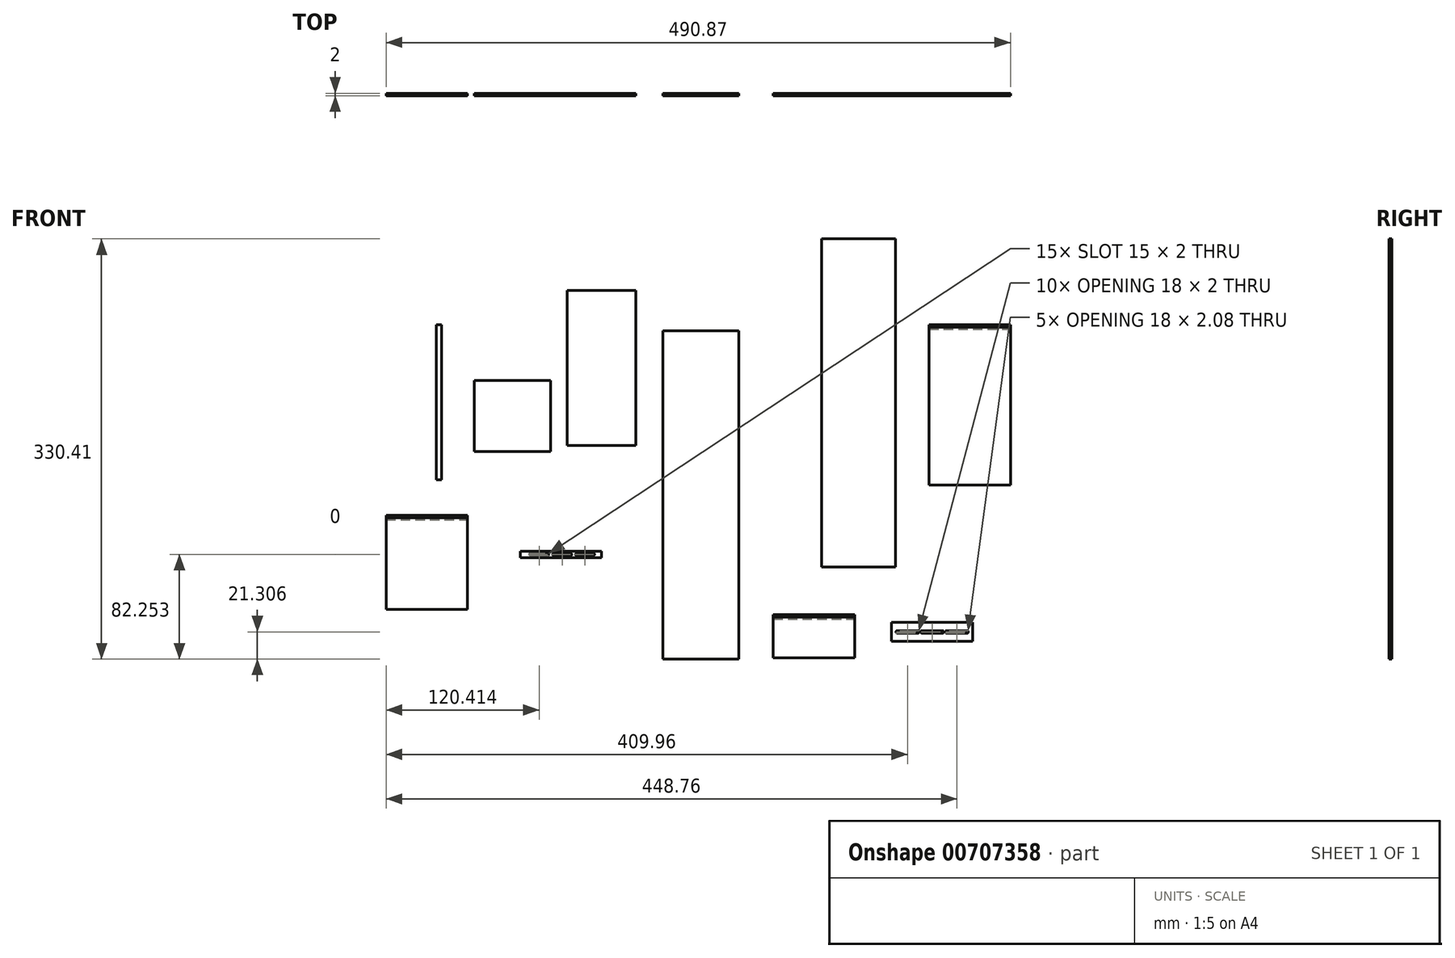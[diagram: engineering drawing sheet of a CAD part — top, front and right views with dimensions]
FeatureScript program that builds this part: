
annotation { "Feature Type Name" : "Feature", "Feature Type Description" : "" }
export const myFeature = defineFeature(function(context is Context, id is Id, definition is map)
    precondition{}
    {
        {
            var Q0;
            Q0=qCreatedBy(makeId("Front.planeOp"),FACE);
            var sketch = newSketch(context, id + "F0", { "sketchPlane" : qUnion([Q0])});
            skLineSegment(sketch, "E0.bottom", {"start": v(-75.81, 223.14) * mm, "end": v(-15.81, 223.14) * mm});
            skLineSegment(sketch, "E0.top", {"start": v(-75.81, -34.86) * mm, "end": v(-15.81, -34.86) * mm});
            skLineSegment(sketch, "E0.left", {"start": v(-75.81, 223.14) * mm, "end": v(-75.81, -34.86) * mm});
            skLineSegment(sketch, "E0.right", {"start": v(-15.81, 223.14) * mm, "end": v(-15.81, -34.86) * mm});
            skSolve(sketch);
        }
        {
            var Q0;
            Q0=makeQuery(id+"F0.imprint","IMPRINT",FACE,{"disambiguationData":[TD([[makeQuery(id+"F0.imprint","IMPRINT",EDGE,{"derivedFrom":sQuery(id+"F0.wireOp",EDGE,"E0.bottom")}),-1.0]])]});
            extrude(context, id + "F1", {"entities" : qUnion([Q0]), "depth" : 2 * mm});
        }
        {
            var Q0;
            Q0=qCreatedBy(makeId("Front.planeOp"),FACE);
            var sketch = newSketch(context, id + "F2", { "sketchPlane" : qUnion([Q0])});
            skLineSegment(sketch, "E1.bottom", {"start": v(49.18, 295.55) * mm, "end": v(107.18, 295.55) * mm});
            skLineSegment(sketch, "E1.top", {"start": v(49.18, 37.55) * mm, "end": v(107.18, 37.55) * mm});
            skLineSegment(sketch, "E1.left", {"start": v(49.18, 295.55) * mm, "end": v(49.18, 37.55) * mm});
            skLineSegment(sketch, "E1.right", {"start": v(107.18, 295.55) * mm, "end": v(107.18, 37.55) * mm});
            skSolve(sketch);
        }
        {
            var Q0;
            Q0=qSketchRegion(id+"F2",true);
            extrude(context, id + "F3", {"entities" : qUnion([Q0]), "depth" : 2 * mm});
        }
        {
            var Q0;
            Q0=qCreatedBy(makeId("Front.planeOp"),FACE);
            var sketch = newSketch(context, id + "F4", { "sketchPlane" : qUnion([Q0])});
            skLineSegment(sketch, "E2.bottom", {"start": v(-223.94, 184.27) * mm, "end": v(-163.94, 184.27) * mm});
            skLineSegment(sketch, "E2.top", {"start": v(-223.94, 128.27) * mm, "end": v(-163.94, 128.27) * mm});
            skLineSegment(sketch, "E2.left", {"start": v(-223.94, 184.27) * mm, "end": v(-223.94, 128.27) * mm});
            skLineSegment(sketch, "E2.right", {"start": v(-163.94, 184.27) * mm, "end": v(-163.94, 128.27) * mm});
            skSolve(sketch);
        }
        {
            var Q0;
            Q0=makeQuery(id+"F4.imprint","IMPRINT",FACE,{"disambiguationData":[TD([[makeQuery(id+"F4.imprint","IMPRINT",EDGE,{"derivedFrom":sQuery(id+"F4.wireOp",EDGE,"E2.bottom")}),-1.0]])]});
            extrude(context, id + "F5", {"entities" : qUnion([Q0]), "depth" : 2 * mm});
        }
        {
            var Q0;
            Q0=qCreatedBy(makeId("Front.planeOp"),FACE);
            var sketch = newSketch(context, id + "F6", { "sketchPlane" : qUnion([Q0])});
            skLineSegment(sketch, "E3.bottom", {"start": v(-187.77, 49.9) * mm, "end": v(-123.77, 49.9) * mm});
            skLineSegment(sketch, "E3.top", {"start": v(-187.77, 44.9) * mm, "end": v(-123.77, 44.9) * mm});
            skLineSegment(sketch, "E3.left", {"start": v(-187.77, 49.9) * mm, "end": v(-187.77, 44.9) * mm});
            skLineSegment(sketch, "E3.right", {"start": v(-123.77, 49.9) * mm, "end": v(-123.77, 44.9) * mm});
            skLineSegment(sketch, "E4.bottom", {"start": v(-179.36, 48.4) * mm, "end": v(-166.36, 48.4) * mm});
            skLineSegment(sketch, "E4.top", {"start": v(-179.36, 46.4) * mm, "end": v(-166.36, 46.4) * mm});
            skLineSegment(sketch, "E4.left", {"start": v(-180.36, 47.4) * mm, "end": v(-180.36, 47.4) * mm});
            skLineSegment(sketch, "E4.right", {"start": v(-165.36, 47.4) * mm, "end": v(-165.36, 47.4) * mm});
            skPoint(sketch, "E5.visualSharp", {"position": v(-180.36, 48.4) * mm});
            skArc(sketch, "E5.filletArc", {"start": v(-179.36, 48.4) * mm, "mid": v(-180.06, 48.1) * mm, "end": v(-180.36, 47.4) * mm});
            skPoint(sketch, "E6.visualSharp", {"position": v(-165.36, 48.4) * mm});
            skArc(sketch, "E6.filletArc", {"start": v(-165.36, 47.4) * mm, "mid": v(-165.65, 48.1) * mm, "end": v(-166.36, 48.4) * mm});
            skPoint(sketch, "E7.visualSharp", {"position": v(-165.36, 46.4) * mm});
            skArc(sketch, "E7.filletArc", {"start": v(-166.36, 46.4) * mm, "mid": v(-165.65, 46.69) * mm, "end": v(-165.36, 47.4) * mm});
            skPoint(sketch, "E8.visualSharp", {"position": v(-180.36, 46.4) * mm});
            skArc(sketch, "E8.filletArc", {"start": v(-180.36, 47.4) * mm, "mid": v(-180.06, 46.69) * mm, "end": v(-179.36, 46.4) * mm});
            skArc(sketch, "E9.1.0.0", {"start": v(-161.36, 48.4) * mm, "mid": v(-162.06, 48.1) * mm, "end": v(-162.36, 47.4) * mm});
            skLineSegment(sketch, "E9.1.0.1", {"start": v(-161.36, 48.4) * mm, "end": v(-148.36, 48.4) * mm});
            skArc(sketch, "E9.1.0.2", {"start": v(-147.36, 47.4) * mm, "mid": v(-147.65, 48.1) * mm, "end": v(-148.36, 48.4) * mm});
            skArc(sketch, "E9.1.0.3", {"start": v(-148.36, 46.4) * mm, "mid": v(-147.65, 46.69) * mm, "end": v(-147.36, 47.4) * mm});
            skLineSegment(sketch, "E9.1.0.4", {"start": v(-161.36, 46.4) * mm, "end": v(-148.36, 46.4) * mm});
            skArc(sketch, "E9.1.0.5", {"start": v(-162.36, 47.4) * mm, "mid": v(-162.06, 46.69) * mm, "end": v(-161.36, 46.4) * mm});
            skArc(sketch, "E9.2.0.0", {"start": v(-143.36, 48.4) * mm, "mid": v(-144.06, 48.1) * mm, "end": v(-144.36, 47.4) * mm});
            skLineSegment(sketch, "E9.2.0.1", {"start": v(-143.36, 48.4) * mm, "end": v(-130.36, 48.4) * mm});
            skArc(sketch, "E9.2.0.2", {"start": v(-129.36, 47.4) * mm, "mid": v(-129.65, 48.1) * mm, "end": v(-130.36, 48.4) * mm});
            skArc(sketch, "E9.2.0.3", {"start": v(-130.36, 46.4) * mm, "mid": v(-129.65, 46.69) * mm, "end": v(-129.36, 47.4) * mm});
            skLineSegment(sketch, "E9.2.0.4", {"start": v(-143.36, 46.4) * mm, "end": v(-130.36, 46.4) * mm});
            skArc(sketch, "E9.2.0.5", {"start": v(-144.36, 47.4) * mm, "mid": v(-144.06, 46.69) * mm, "end": v(-143.36, 46.4) * mm});
            skLineSegment(sketch, "E9.direction1", {"start": v(-180.36, 47.4) * mm, "end": v(-162.36, 47.4) * mm, "construction": true});
            skSolve(sketch);
        }
        {
            var Q0;
            Q0=qSketchRegion(id+"F6",true);
            extrude(context, id + "F7", {"entities" : qUnion([Q0]), "depth" : 2 * mm});
        }
        {
            var Q0;
            Q0=qCreatedBy(makeId("Front.planeOp"),FACE);
            var sketch = newSketch(context, id + "F8", { "sketchPlane" : qUnion([Q0])});
            skLineSegment(sketch, "E10.bottom", {"start": v(-293.27, 78.23) * mm, "end": v(-229.27, 78.23) * mm});
            skLineSegment(sketch, "E10.top", {"start": v(-293.27, 4.23) * mm, "end": v(-229.27, 4.23) * mm});
            skLineSegment(sketch, "E10.left", {"start": v(-293.27, 78.23) * mm, "end": v(-293.27, 4.23) * mm});
            skLineSegment(sketch, "E10.right", {"start": v(-229.27, 78.23) * mm, "end": v(-229.27, 4.23) * mm});
            skSolve(sketch);
        }
        {
            var Q0;
            Q0=makeQuery(id+"F8.imprint","IMPRINT",FACE,{"disambiguationData":[TD([[makeQuery(id+"F8.imprint","IMPRINT",EDGE,{"derivedFrom":sQuery(id+"F8.wireOp",EDGE,"E10.bottom")}),-1.0]])]});
            extrude(context, id + "F9", {"entities" : qUnion([Q0]), "depth" : 2 * mm});
        }
        {
            var Q0;
            Q0=qCreatedBy(makeId("Front.planeOp"),FACE);
            var sketch = newSketch(context, id + "F10", { "sketchPlane" : qUnion([Q0])});
            skLineSegment(sketch, "E11.bottom", {"start": v(104.02, -5.93) * mm, "end": v(168.02, -5.93) * mm});
            skLineSegment(sketch, "E11.top", {"start": v(104.02, -20.93) * mm, "end": v(168.02, -20.93) * mm});
            skLineSegment(sketch, "E11.left", {"start": v(104.02, -5.93) * mm, "end": v(104.02, -20.93) * mm});
            skLineSegment(sketch, "E11.right", {"start": v(168.02, -5.93) * mm, "end": v(168.02, -20.93) * mm});
            skSolve(sketch);
        }
        {
            var Q0;
            Q0=qSketchRegion(id+"F10",true);
            extrude(context, id + "F11", {"entities" : qUnion([Q0]), "depth" : 2 * mm});
        }
        {
            var Q0;
            Q0=qCreatedBy(makeId("Front.planeOp"),FACE);
            var sketch = newSketch(context, id + "F12", { "sketchPlane" : qUnion([Q0])});
            skLineSegment(sketch, "E12.bottom", {"start": v(108.46, -12.55) * mm, "end": v(124.92, -12.55) * mm});
            skLineSegment(sketch, "E12.top", {"start": v(108.46, -14.55) * mm, "end": v(124.92, -14.55) * mm});
            skLineSegment(sketch, "E12.left", {"start": v(107.69, -13.33) * mm, "end": v(107.69, -13.78) * mm});
            skLineSegment(sketch, "E12.right", {"start": v(125.69, -13.33) * mm, "end": v(125.69, -13.78) * mm});
            skLineSegment(sketch, "E13.1.0.0", {"start": v(127.86, -12.55) * mm, "end": v(144.32, -12.55) * mm});
            skLineSegment(sketch, "E13.1.0.1", {"start": v(127.86, -14.55) * mm, "end": v(144.32, -14.55) * mm});
            skLineSegment(sketch, "E13.1.0.2", {"start": v(127.09, -13.33) * mm, "end": v(127.09, -13.78) * mm});
            skLineSegment(sketch, "E13.1.0.3", {"start": v(145.09, -13.33) * mm, "end": v(145.09, -13.78) * mm});
            skLineSegment(sketch, "E13.2.0.0", {"start": v(147.26, -12.51) * mm, "end": v(163.72, -12.51) * mm});
            skLineSegment(sketch, "E13.2.0.1", {"start": v(147.26, -14.6) * mm, "end": v(163.72, -14.6) * mm});
            skLineSegment(sketch, "E13.2.0.2", {"start": v(146.49, -13.29) * mm, "end": v(146.49, -13.82) * mm});
            skLineSegment(sketch, "E13.2.0.3", {"start": v(164.49, -13.29) * mm, "end": v(164.49, -13.82) * mm});
            skLineSegment(sketch, "E13.direction1", {"start": v(107.69, -14.55) * mm, "end": v(127.09, -14.55) * mm, "construction": true});
            skPoint(sketch, "E14.visualSharp", {"position": v(107.69, -12.55) * mm});
            skArc(sketch, "E14.filletArc", {"start": v(108.46, -12.55) * mm, "mid": v(107.92, -12.78) * mm, "end": v(107.69, -13.33) * mm});
            skPoint(sketch, "E15.visualSharp", {"position": v(125.69, -12.55) * mm});
            skArc(sketch, "E15.filletArc", {"start": v(125.69, -13.33) * mm, "mid": v(125.46, -12.78) * mm, "end": v(124.92, -12.55) * mm});
            skPoint(sketch, "E16.visualSharp", {"position": v(125.69, -14.55) * mm});
            skArc(sketch, "E16.filletArc", {"start": v(124.92, -14.55) * mm, "mid": v(125.46, -14.33) * mm, "end": v(125.69, -13.78) * mm});
            skPoint(sketch, "E17.visualSharp", {"position": v(107.69, -14.55) * mm});
            skArc(sketch, "E17.filletArc", {"start": v(107.69, -13.78) * mm, "mid": v(107.92, -14.33) * mm, "end": v(108.46, -14.55) * mm});
            skPoint(sketch, "E18.visualSharp", {"position": v(127.09, -12.55) * mm});
            skArc(sketch, "E18.filletArc", {"start": v(127.86, -12.55) * mm, "mid": v(127.32, -12.78) * mm, "end": v(127.09, -13.33) * mm});
            skPoint(sketch, "E19.visualSharp", {"position": v(145.09, -12.55) * mm});
            skArc(sketch, "E19.filletArc", {"start": v(145.09, -13.33) * mm, "mid": v(144.86, -12.78) * mm, "end": v(144.32, -12.55) * mm});
            skPoint(sketch, "E20.visualSharp", {"position": v(145.09, -14.55) * mm});
            skArc(sketch, "E20.filletArc", {"start": v(144.32, -14.55) * mm, "mid": v(144.86, -14.33) * mm, "end": v(145.09, -13.78) * mm});
            skPoint(sketch, "E21.visualSharp", {"position": v(127.09, -14.55) * mm});
            skArc(sketch, "E21.filletArc", {"start": v(127.09, -13.78) * mm, "mid": v(127.32, -14.33) * mm, "end": v(127.86, -14.55) * mm});
            skPoint(sketch, "E22.visualSharp", {"position": v(146.49, -12.51) * mm});
            skArc(sketch, "E22.filletArc", {"start": v(147.26, -12.51) * mm, "mid": v(146.72, -12.74) * mm, "end": v(146.49, -13.29) * mm});
            skPoint(sketch, "E23.visualSharp", {"position": v(146.49, -14.6) * mm});
            skArc(sketch, "E23.filletArc", {"start": v(146.49, -13.82) * mm, "mid": v(146.72, -14.37) * mm, "end": v(147.26, -14.6) * mm});
            skPoint(sketch, "E24.visualSharp", {"position": v(164.49, -12.51) * mm});
            skArc(sketch, "E24.filletArc", {"start": v(164.49, -13.29) * mm, "mid": v(164.26, -12.74) * mm, "end": v(163.72, -12.51) * mm});
            skPoint(sketch, "E25.visualSharp", {"position": v(164.49, -14.6) * mm});
            skArc(sketch, "E25.filletArc", {"start": v(163.72, -14.6) * mm, "mid": v(164.26, -14.37) * mm, "end": v(164.49, -13.82) * mm});
            skSolve(sketch);
        }
        {
            var Q0;
            Q0=qSketchRegion(id+"F12",true);
            extrude(context, id + "F13", {"entities" : qUnion([Q0]), "operationType" : NewBodyOperationType.REMOVE, "depth" : 4 * mm});
        }
        {
            var Q0;
            Q0=qCreatedBy(makeId("Front.planeOp"),FACE);
            var sketch = newSketch(context, id + "F14", { "sketchPlane" : qUnion([Q0])});
            skLineSegment(sketch, "E26.bottom", {"start": v(133.6, 228.09) * mm, "end": v(197.6, 228.09) * mm});
            skLineSegment(sketch, "E26.top", {"start": v(133.6, 102.09) * mm, "end": v(197.6, 102.09) * mm});
            skLineSegment(sketch, "E26.left", {"start": v(133.6, 228.09) * mm, "end": v(133.6, 102.09) * mm});
            skLineSegment(sketch, "E26.right", {"start": v(197.6, 228.09) * mm, "end": v(197.6, 102.09) * mm});
            skSolve(sketch);
        }
        {
            var Q0;
            Q0=makeQuery(id+"F14.imprint","IMPRINT",FACE,{"disambiguationData":[TD([[makeQuery(id+"F14.imprint","IMPRINT",EDGE,{"derivedFrom":sQuery(id+"F14.wireOp",EDGE,"E26.bottom")}),-1.0]])]});
            extrude(context, id + "F15", {"entities" : qUnion([Q0]), "depth" : 2 * mm});
        }
        {
            var Q0;
            Q0=qCreatedBy(makeId("Front.planeOp"),FACE);
            var sketch = newSketch(context, id + "F16", { "sketchPlane" : qUnion([Q0])});
            skLineSegment(sketch, "E27.bottom", {"start": v(11.1, 0.17) * mm, "end": v(75.1, 0.17) * mm});
            skLineSegment(sketch, "E27.top", {"start": v(11.1, -33.83) * mm, "end": v(75.1, -33.83) * mm});
            skLineSegment(sketch, "E27.left", {"start": v(11.1, 0.17) * mm, "end": v(11.1, -33.83) * mm});
            skLineSegment(sketch, "E27.right", {"start": v(75.1, 0.17) * mm, "end": v(75.1, -33.83) * mm});
            skSolve(sketch);
        }
        {
            var Q0;
            Q0=qSketchRegion(id+"F16",true);
            extrude(context, id + "F17", {"entities" : qUnion([Q0]), "operationType" : NewBodyOperationType.ADD, "depth" : 2 * mm});
        }
        {
            var Q0;
            Q0=qCreatedBy(makeId("Front.planeOp"),FACE);
            var sketch = newSketch(context, id + "F18", { "sketchPlane" : qUnion([Q0])});
            skLineSegment(sketch, "E28.bottom", {"start": v(-150.94, 255.06) * mm, "end": v(-96.94, 255.06) * mm});
            skLineSegment(sketch, "E28.top", {"start": v(-150.94, 133.06) * mm, "end": v(-96.94, 133.06) * mm});
            skLineSegment(sketch, "E28.left", {"start": v(-150.94, 255.06) * mm, "end": v(-150.94, 133.06) * mm});
            skLineSegment(sketch, "E28.right", {"start": v(-96.94, 255.06) * mm, "end": v(-96.94, 133.06) * mm});
            skSolve(sketch);
        }
        {
            var Q0;
            Q0=qSketchRegion(id+"F18",true);
            extrude(context, id + "F19", {"entities" : qUnion([Q0]), "depth" : 2 * mm});
        }
        {
            var Q0;
            Q0=qCreatedBy(makeId("Front.planeOp"),FACE);
            var sketch = newSketch(context, id + "F20", { "sketchPlane" : qUnion([Q0])});
            skLineSegment(sketch, "E29.bottom", {"start": v(-253.8, 228.05) * mm, "end": v(-249.8, 228.05) * mm});
            skLineSegment(sketch, "E29.top", {"start": v(-253.8, 106.05) * mm, "end": v(-249.8, 106.05) * mm});
            skLineSegment(sketch, "E29.left", {"start": v(-253.8, 228.05) * mm, "end": v(-253.8, 106.05) * mm});
            skLineSegment(sketch, "E29.right", {"start": v(-249.8, 228.05) * mm, "end": v(-249.8, 106.05) * mm});
            skSolve(sketch);
        }
        {
            var Q0;
            Q0=qSketchRegion(id+"F20",true);
            extrude(context, id + "F21", {"entities" : qUnion([Q0]), "depth" : 2 * mm});
        }
        {
            var Q0;
            Q0=makeQuery(id+"F9.opExtrude","SWEPT_FACE",FACE,{"disambiguationData":[OSD([sQuery(id+"F8.wireOp",EDGE,"E10.right")])]});
            var sketch = newSketch(context, id + "F22", { "sketchPlane" : qUnion([Q0])});
            skLineSegment(sketch, "E30", {"start": v(-2, 78.23) * mm, "end": v(-2, 76.23) * mm});
            skLineSegment(sketch, "E31", {"start": v(-2, 76.23) * mm, "end": v(-1.5, 76.23) * mm});
            skLineSegment(sketch, "E32", {"start": v(-1.5, 76.23) * mm, "end": v(-1.5, 75.73) * mm});
            skLineSegment(sketch, "E33", {"start": v(-0.5, 74.73) * mm, "end": v(-0.5, 74.73) * mm});
            skLineSegment(sketch, "E34", {"start": v(-0.5, 74.73) * mm, "end": v(-0.5, 78.23) * mm});
            skLineSegment(sketch, "E35", {"start": v(-0.5, 78.23) * mm, "end": v(-2, 78.23) * mm});
            skPoint(sketch, "E36.visualSharp", {"position": v(-1.5, 74.73) * mm});
            skArc(sketch, "E36.filletArc", {"start": v(-1.5, 75.73) * mm, "mid": v(-1.2, 75.02) * mm, "end": v(-0.5, 74.73) * mm});
            skSolve(sketch);
        }
        {
            var Q0;
            Q0=qSketchRegion(id+"F22",true);
            extrude(context, id + "F23", {"entities" : qUnion([Q0]), "operationType" : NewBodyOperationType.REMOVE, "oppositeDirection" : true, "depth" : 64 * mm});
        }
        {
            var Q0;
            Q0=makeQuery(id+"F23.boolean.opBoolean","COPY",EDGE,{"derivedFrom":makeQuery(id+"F23.opExtrude","SWEPT_EDGE",EDGE,{"disambiguationData":[OSD([sQuery(id+"F8.wireOp",EDGE,"E10.bottom"),sQuery(id+"F8.wireOp",EDGE,"E10.right"),sQuery(id+"F22.wireOp",EDGE,"E34"),sQuery(id+"F22.wireOp",EDGE,"E35")])]})});
            var Q1;
            Q1=makeQuery(id+"F23.boolean.opBoolean","COPY",EDGE,{"derivedFrom":makeQuery(id+"F23.opExtrude","SWEPT_EDGE",EDGE,{"disambiguationData":[OSD([sQuery(id+"F8.wireOp",EDGE,"E10.right"),sQuery(id+"F22.wireOp",EDGE,"E30"),sQuery(id+"F22.wireOp",EDGE,"E31")])]})});
            var Q2;
            Q2=makeQuery(id+"F23.boolean.opBoolean","COPY",EDGE,{"derivedFrom":makeQuery(id+"F23.opExtrude","SWEPT_EDGE",EDGE,{"disambiguationData":[OSD([sQuery(id+"F22.wireOp",EDGE,"E31"),sQuery(id+"F22.wireOp",EDGE,"E36.filletArc")])]})});
            fillet(context, id + "F24", {"entities" : qUnion([Q0, Q1, Q2]), "radius" : 0.2 * mm, "tangentPropagation" : true, "allowEdgeOverflow" : false});
        }
        {
            var Q0;
            Q0=makeQuery(id+"F15.opExtrude","SWEPT_FACE",FACE,{"disambiguationData":[OSD([sQuery(id+"F14.wireOp",EDGE,"E26.right")])]});
            var sketch = newSketch(context, id + "F25", { "sketchPlane" : qUnion([Q0])});
            skLineSegment(sketch, "E37", {"start": v(-2, 228.09) * mm, "end": v(-2, 226.09) * mm});
            skLineSegment(sketch, "E38", {"start": v(-2, 226.09) * mm, "end": v(-1.5, 226.09) * mm});
            skLineSegment(sketch, "E39", {"start": v(-1.5, 226.09) * mm, "end": v(-1.5, 225.59) * mm});
            skLineSegment(sketch, "E40", {"start": v(-0.5, 224.59) * mm, "end": v(-0.5, 224.59) * mm});
            skLineSegment(sketch, "E41", {"start": v(-0.5, 224.59) * mm, "end": v(-0.5, 228.09) * mm});
            skLineSegment(sketch, "E42", {"start": v(-0.5, 228.09) * mm, "end": v(-2, 228.09) * mm});
            skPoint(sketch, "E43.visualSharp", {"position": v(-1.5, 224.59) * mm});
            skArc(sketch, "E43.filletArc", {"start": v(-1.5, 225.59) * mm, "mid": v(-1.2, 224.88) * mm, "end": v(-0.5, 224.59) * mm});
            skSolve(sketch);
        }
        {
            var Q0;
            Q0=qSketchRegion(id+"F25",true);
            extrude(context, id + "F26", {"entities" : qUnion([Q0]), "operationType" : NewBodyOperationType.REMOVE, "oppositeDirection" : true, "depth" : 64 * mm});
        }
        {
            var Q0;
            Q0=makeQuery(id+"F26.boolean.opBoolean","COPY",EDGE,{"derivedFrom":makeQuery(id+"F26.opExtrude","SWEPT_EDGE",EDGE,{"disambiguationData":[OSD([sQuery(id+"F14.wireOp",EDGE,"E26.bottom"),sQuery(id+"F14.wireOp",EDGE,"E26.right"),sQuery(id+"F25.wireOp",EDGE,"E41"),sQuery(id+"F25.wireOp",EDGE,"E42")])]})});
            var Q1;
            Q1=makeQuery(id+"F26.boolean.opBoolean","COPY",EDGE,{"derivedFrom":makeQuery(id+"F26.opExtrude","SWEPT_EDGE",EDGE,{"disambiguationData":[OSD([sQuery(id+"F14.wireOp",EDGE,"E26.right"),sQuery(id+"F25.wireOp",EDGE,"E37"),sQuery(id+"F25.wireOp",EDGE,"E38")])]})});
            var Q2;
            Q2=makeQuery(id+"F26.boolean.opBoolean","COPY",EDGE,{"derivedFrom":makeQuery(id+"F26.opExtrude","SWEPT_EDGE",EDGE,{"disambiguationData":[OSD([sQuery(id+"F25.wireOp",EDGE,"E38"),sQuery(id+"F25.wireOp",EDGE,"E39")])]})});
            fillet(context, id + "F27", {"entities" : qUnion([Q0, Q1, Q2]), "radius" : 0.2 * mm, "tangentPropagation" : true, "allowEdgeOverflow" : false});
        }
        {
            var Q0;
            Q0=makeQuery(id+"F17.opExtrude","SWEPT_FACE",FACE,{"disambiguationData":[OSD([sQuery(id+"F16.wireOp",EDGE,"E27.right")])]});
            var sketch = newSketch(context, id + "F28", { "sketchPlane" : qUnion([Q0])});
            skLineSegment(sketch, "E44", {"start": v(-2, 0.17) * mm, "end": v(-2, -1.83) * mm});
            skLineSegment(sketch, "E45", {"start": v(-2, -1.83) * mm, "end": v(-1.5, -1.83) * mm});
            skLineSegment(sketch, "E46", {"start": v(-1.5, -1.83) * mm, "end": v(-1.5, -2.33) * mm});
            skLineSegment(sketch, "E47", {"start": v(-0.5, -3.33) * mm, "end": v(-0.5, -3.33) * mm});
            skLineSegment(sketch, "E48", {"start": v(-0.5, -3.33) * mm, "end": v(-0.5, 0.17) * mm});
            skLineSegment(sketch, "E49", {"start": v(-0.5, 0.17) * mm, "end": v(-2, 0.17) * mm});
            skPoint(sketch, "E50.visualSharp", {"position": v(-1.5, -3.33) * mm});
            skArc(sketch, "E50.filletArc", {"start": v(-1.5, -2.33) * mm, "mid": v(-1.2, -3.04) * mm, "end": v(-0.5, -3.33) * mm});
            skSolve(sketch);
        }
        {
            var Q0;
            Q0=qSketchRegion(id+"F28",true);
            extrude(context, id + "F29", {"entities" : qUnion([Q0]), "operationType" : NewBodyOperationType.REMOVE, "oppositeDirection" : true, "depth" : 64 * mm});
        }
        {
            var Q0;
            Q0=makeQuery(id+"F29.boolean.opBoolean","COPY",EDGE,{"derivedFrom":makeQuery(id+"F29.opExtrude","SWEPT_EDGE",EDGE,{"disambiguationData":[OSD([sQuery(id+"F16.wireOp",EDGE,"E27.bottom"),sQuery(id+"F16.wireOp",EDGE,"E27.right"),sQuery(id+"F28.wireOp",EDGE,"E48"),sQuery(id+"F28.wireOp",EDGE,"E49")])]})});
            var Q1;
            Q1=makeQuery(id+"F29.boolean.opBoolean","COPY",EDGE,{"derivedFrom":makeQuery(id+"F29.opExtrude","SWEPT_EDGE",EDGE,{"disambiguationData":[OSD([sQuery(id+"F28.wireOp",EDGE,"E45"),sQuery(id+"F28.wireOp",EDGE,"E46")])]})});
            var Q2;
            Q2=makeQuery(id+"F29.boolean.opBoolean","COPY",EDGE,{"derivedFrom":makeQuery(id+"F29.opExtrude","SWEPT_EDGE",EDGE,{"disambiguationData":[OSD([sQuery(id+"F16.wireOp",EDGE,"E27.right"),sQuery(id+"F28.wireOp",EDGE,"E44"),sQuery(id+"F28.wireOp",EDGE,"E45")])]})});
            fillet(context, id + "F30", {"entities" : qUnion([Q0, Q1, Q2]), "radius" : 0.2 * mm, "tangentPropagation" : true, "allowEdgeOverflow" : false});
        }
    });
